# Revit family: Maxlogic Оповещатели световые, звуковые, светозвуковые (Низкий класс защиты IP)
name_source: partatom
category: Fire Alarm Devices
units: mm (PartAtom-declared; Revit-internal decimal feet)

## family parameters
Cut with Voids When Loaded = No
Host = Face
Maintain Annotation Orientation = Yes
OmniClass Number = 23.85.30.21
OmniClass Title = Environmental Detection/Registration
Part Type = Normal
Room Calculation Point = No
Round Connector Dimension = Use Diameter
Shared = No

## types (9) — shared parameters
Manufacturer = Mavili Elektronik Ticaret A.Ş.
Model = MaxLogic
URL = https://www.mavili.com.tr
Адрес №1 = Şerifali Mahallesi Kutup Sokak No:27/1-2-4 Ümraniye TR-34775 İSTANBUL
Вторичный материал = Пластмассовый
Гарантийный срок = Года
Гарантийный срок запчастей = 2
Гарантия срока службы = 2
Главный Материал = Красный пластмассовый ABS
Инструкция по установке = https://mavilielektronik.com
Класс защиты = IP21C
Монтажная высота = Выше пола на 240 см
Монтажная поверхность = Настенная
Номер телефона = (+)90 216 466 45 05
Номер факса = (+)90 216 466 45 10
Номинальная высота = 122 мм
Номинальная ширина = 122 мм
Рабочая Температура = (-10°C) - (+55°C)
Рабочее напряжение (по умолчанию) = 24 В Пост. ток
Цвет = Красный
zero-valued in all types: Cost, Default Elevation

## per-type parameters (varying)
| type | Description | Вес | Диапазон рабочего напряжения | Код продукта | Настройка адреса устройства | Номер позы общественных работ | Номинальная глубина | Производительность кода | световой |
| Maxlogic Неадресный оповещатель пожарный звуковой | Неадресный оповещатель пожарный звуковой | 195 гр | 21-28 В Пост. ток | ML-2410 |  | 833-590 | 90 мм | EN 54-3 | No |
| Maxlogic Неадресный оповещатель пожарный световой | Неадресный оповещатель пожарный световой | 205 гр | 21-28 В Пост. ток | ML-2420 |  | 833-591 | 101,5 мм | EN 54-23 | Yes |
| Maxlogic Неадресный оповещатель пожарный светозвуковой | Неадресный оповещатель пожарный светозвуковой | 220 гр | 21-28 В Пост. ток | ML-2430 |  | 833-592 | 101,5 мм | EN 54-3 / EN 54-23 | Yes |
| Maxlogic Адресный звуковой оповещатель | Адресный звуковой оповещатель | 186 гр | 18-33 В Пост. ток | ML-1410 | Модульная адресация |  | 90 мм | EN 54-3 | No |
| Maxlogic Адресный звуковой оповещатель, с изолятором КЗ | Адресный звуковой оповещатель, с изолятором КЗ | 186 гр | 18-33 В Пост. ток | ML-1410.SCI | Модульная адресация |  | 90 мм | EN 54-3 | No |
| Maxlogic Адресный световой оповещатель | Адресный световой оповещатель | 201 гр | 18-33 В Пост. ток | ML-1420 | Модульная адресация |  | 90 мм | EN 54-23 | Yes |
| Maxlogic  Адресный световой оповещатель, с изолятором КЗ | Адресный световой оповещатель, с изолятором КЗ | 201 гр | 18-33 В Пост. ток | ML-1420.SCI | Модульная адресация |  | 90 мм | EN 54-23 | Yes |
| Maxlogic Адресный светозвуковой оповещатель | Адресный светозвуковой оповещатель | 217 гр | 18-33 В Пост. ток | ML-1430 | Модульная адресация |  | 90 мм | EN 54-3 / EN 54-23 | Yes |
| Maxlogic Адресный светозвуковой оповещатель, с изолятором КЗ | Адресный светозвуковой оповещатель, с изолятором КЗ | 217 гр | 18-33 В Пост. ток | ML-1430.SCI | Модульная адресация |  | 90 мм | EN 54-3 / EN 54-23 | Yes |

## geometry (parser evidence)
native form markers: Sweep x5
no freeform markers — native parametric forms only
